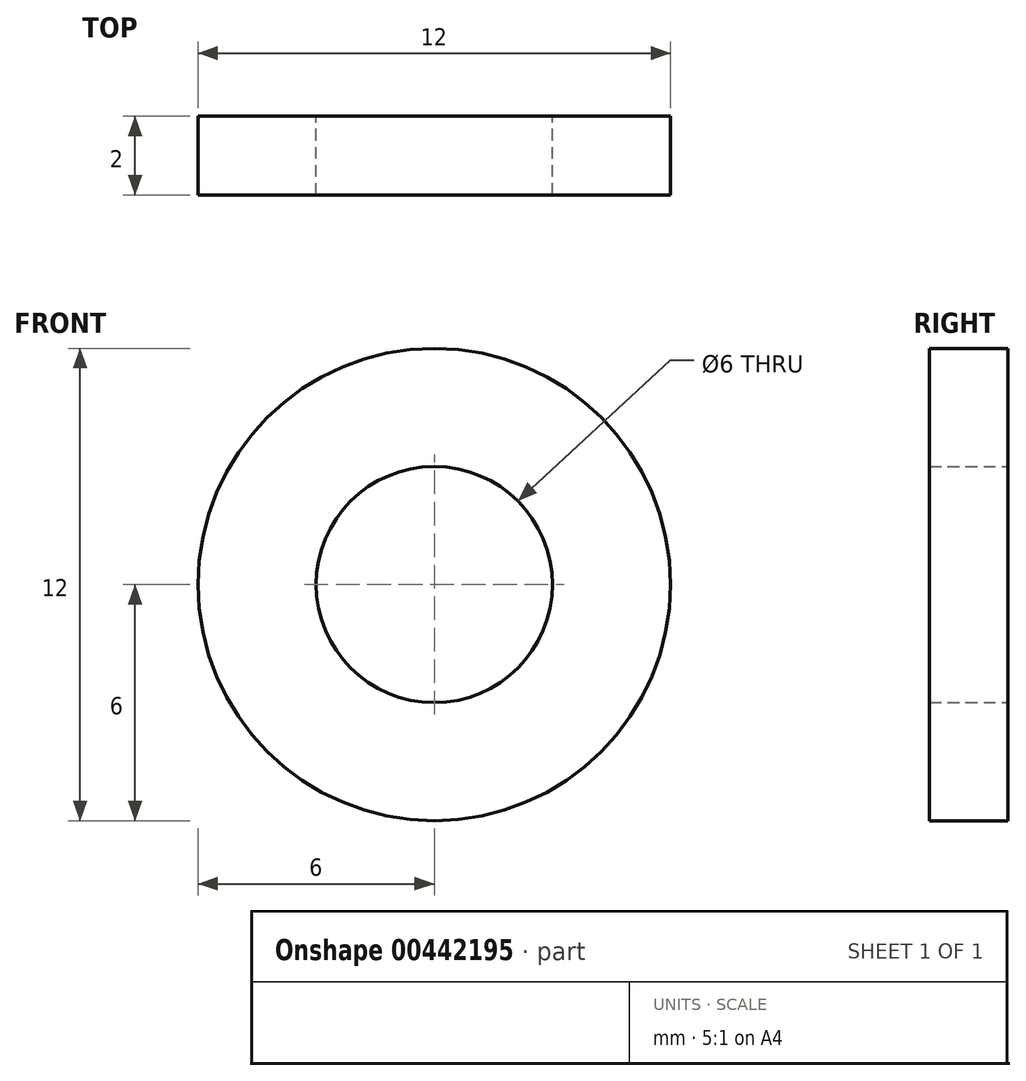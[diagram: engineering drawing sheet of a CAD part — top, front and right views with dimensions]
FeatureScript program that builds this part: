
annotation { "Feature Type Name" : "Feature", "Feature Type Description" : "" }
export const myFeature = defineFeature(function(context is Context, id is Id, definition is map)
    precondition{}
    {
        {
            var Q0;
            Q0=qCreatedBy(makeId("Front.planeOp"),FACE);
            var sketch = newSketch(context, id + "F0", { "sketchPlane" : qUnion([Q0])});
            skCircle(sketch, "E0", {"center": v(0, 0) * mm, "radius": 3 * mm});
            skCircle(sketch, "E1", {"center": v(0, 0) * mm, "radius": 6 * mm});
            skSolve(sketch);
        }
        {
            var Q0;
            Q0=makeQuery(id+"F0.imprint","IMPRINT",FACE,{"disambiguationData":[TD([[makeQuery(id+"F0.imprint","IMPRINT",EDGE,{"derivedFrom":sQuery(id+"F0.wireOp",EDGE,"E0")}),-1.0]])]});
            extrude(context, id + "F1", {"entities" : qUnion([Q0]), "depth" : 2 * mm});
        }
    });
